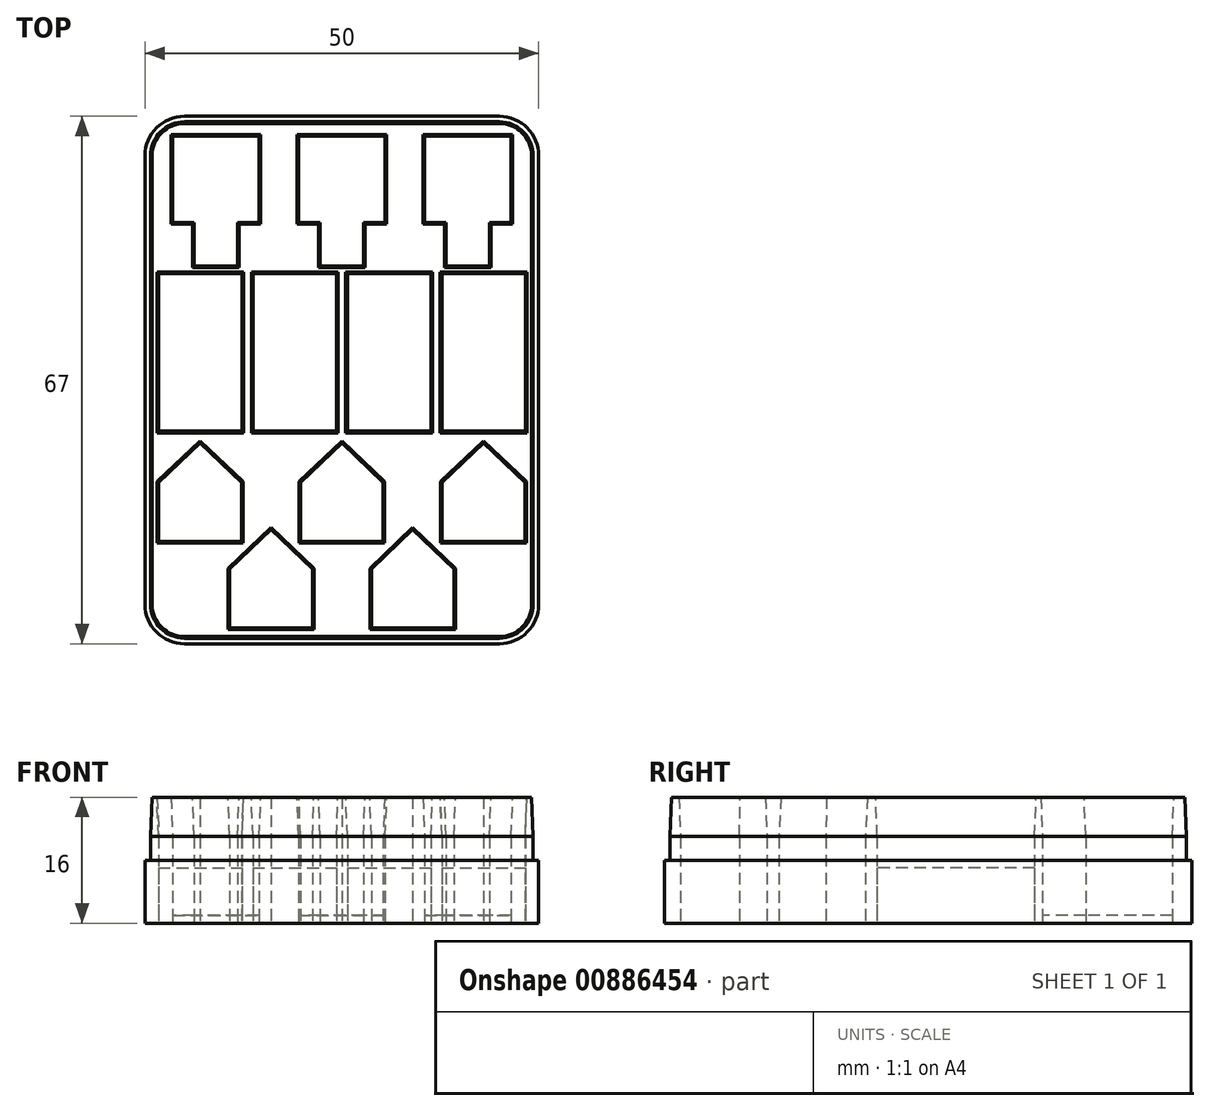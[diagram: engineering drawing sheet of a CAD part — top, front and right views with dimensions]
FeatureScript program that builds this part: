
annotation { "Feature Type Name" : "Feature", "Feature Type Description" : "" }
export const myFeature = defineFeature(function(context is Context, id is Id, definition is map)
    precondition{}
    {
        {
            var Q0;
            Q0=qCreatedBy(makeId("Top.planeOp"),FACE);
            var sketch = newSketch(context, id + "F0", { "sketchPlane" : qUnion([Q0])});
            skLineSegment(sketch, "E0.bottom", {"start": v(20, 33.5) * mm, "end": v(-20, 33.5) * mm});
            skLineSegment(sketch, "E0.top", {"start": v(20, -33.5) * mm, "end": v(-20, -33.5) * mm});
            skLineSegment(sketch, "E0.left", {"start": v(25, 28.5) * mm, "end": v(25, -28.5) * mm});
            skLineSegment(sketch, "E0.right", {"start": v(-25, 28.5) * mm, "end": v(-25, -28.5) * mm});
            skPoint(sketch, "E0.middle", {"position": v(0, 0) * mm});
            skLineSegment(sketch, "E1", {"start": v(-5.5, 31) * mm, "end": v(5.5, 31) * mm});
            skLineSegment(sketch, "E2", {"start": v(5.5, 20) * mm, "end": v(2.75, 20) * mm});
            skLineSegment(sketch, "E3", {"start": v(2.75, 20) * mm, "end": v(2.75, 14.5) * mm});
            skLineSegment(sketch, "E4", {"start": v(2.75, 14.5) * mm, "end": v(-2.75, 14.5) * mm});
            skLineSegment(sketch, "E5", {"start": v(-2.75, 14.5) * mm, "end": v(-2.75, 20) * mm});
            skLineSegment(sketch, "E6", {"start": v(-2.75, 20) * mm, "end": v(-5.5, 20) * mm});
            skLineSegment(sketch, "E7", {"start": v(-5.5, 20) * mm, "end": v(-5.5, 31) * mm});
            skLineSegment(sketch, "E8", {"start": v(5.5, 31) * mm, "end": v(5.5, 20) * mm});
            skLineSegment(sketch, "E9.1.0.0", {"start": v(10.5, 31) * mm, "end": v(21.5, 31) * mm});
            skLineSegment(sketch, "E9.1.0.1", {"start": v(18.75, 14.5) * mm, "end": v(13.25, 14.5) * mm});
            skLineSegment(sketch, "E9.1.0.2", {"start": v(21.5, 31) * mm, "end": v(21.5, 20) * mm});
            skLineSegment(sketch, "E9.1.0.3", {"start": v(21.5, 20) * mm, "end": v(18.75, 20) * mm});
            skLineSegment(sketch, "E9.1.0.4", {"start": v(18.75, 20) * mm, "end": v(18.75, 14.5) * mm});
            skLineSegment(sketch, "E9.1.0.5", {"start": v(13.25, 14.5) * mm, "end": v(13.25, 20) * mm});
            skLineSegment(sketch, "E9.1.0.6", {"start": v(10.5, 20) * mm, "end": v(10.5, 31) * mm});
            skLineSegment(sketch, "E9.1.0.7", {"start": v(13.25, 20) * mm, "end": v(10.5, 20) * mm});
            skLineSegment(sketch, "E9.direction1", {"start": v(-2.75, 14.5) * mm, "end": v(13.25, 14.5) * mm, "construction": true});
            skLineSegment(sketch, "E10.direction1", {"start": v(-2.75, 14.5) * mm, "end": v(-18.75, 14.5) * mm, "construction": true});
            skLineSegment(sketch, "E11.0.1.0", {"start": v(-13.25, 14.5) * mm, "end": v(-18.75, 14.5) * mm});
            skLineSegment(sketch, "E11.3.1.0", {"start": v(-21.5, 31) * mm, "end": v(-10.5, 31) * mm});
            skLineSegment(sketch, "E11.6.1.0", {"start": v(-21.5, 20) * mm, "end": v(-21.5, 31) * mm});
            skLineSegment(sketch, "E11.9.1.0", {"start": v(-18.75, 14.5) * mm, "end": v(-18.75, 20) * mm});
            skLineSegment(sketch, "E11.12.1.0", {"start": v(-10.5, 31) * mm, "end": v(-10.5, 20) * mm});
            skLineSegment(sketch, "E11.15.1.0", {"start": v(-10.5, 20) * mm, "end": v(-13.25, 20) * mm});
            skLineSegment(sketch, "E11.18.1.0", {"start": v(-13.25, 20) * mm, "end": v(-13.25, 14.5) * mm});
            skLineSegment(sketch, "E11.21.1.0", {"start": v(-18.75, 20) * mm, "end": v(-21.5, 20) * mm});
            skLineSegment(sketch, "E12.bottom", {"start": v(-23.3, 13.5) * mm, "end": v(-12.7, 13.5) * mm});
            skLineSegment(sketch, "E12.top", {"start": v(-23.3, -6.5) * mm, "end": v(-12.7, -6.5) * mm});
            skLineSegment(sketch, "E12.left", {"start": v(-23.3, 13.5) * mm, "end": v(-23.3, -6.5) * mm});
            skLineSegment(sketch, "E12.right", {"start": v(-12.7, 13.5) * mm, "end": v(-12.7, -6.5) * mm});
            skLineSegment(sketch, "E13.1.0.0", {"start": v(-11.3, -6.5) * mm, "end": v(-0.7, -6.5) * mm});
            skLineSegment(sketch, "E13.1.0.1", {"start": v(-11.3, 13.5) * mm, "end": v(-0.7, 13.5) * mm});
            skLineSegment(sketch, "E13.1.0.2", {"start": v(-0.7, 13.5) * mm, "end": v(-0.7, -6.5) * mm});
            skLineSegment(sketch, "E13.1.0.3", {"start": v(-11.3, 13.5) * mm, "end": v(-11.3, -6.5) * mm});
            skLineSegment(sketch, "E13.2.0.0", {"start": v(0.7, -6.5) * mm, "end": v(11.3, -6.5) * mm});
            skLineSegment(sketch, "E13.2.0.1", {"start": v(0.7, 13.5) * mm, "end": v(11.3, 13.5) * mm});
            skLineSegment(sketch, "E13.2.0.2", {"start": v(11.3, 13.5) * mm, "end": v(11.3, -6.5) * mm});
            skLineSegment(sketch, "E13.2.0.3", {"start": v(0.7, 13.5) * mm, "end": v(0.7, -6.5) * mm});
            skLineSegment(sketch, "E13.3.0.0", {"start": v(12.7, -6.5) * mm, "end": v(23.3, -6.5) * mm});
            skLineSegment(sketch, "E13.3.0.1", {"start": v(12.7, 13.5) * mm, "end": v(23.3, 13.5) * mm});
            skLineSegment(sketch, "E13.3.0.2", {"start": v(23.3, 13.5) * mm, "end": v(23.3, -6.5) * mm});
            skLineSegment(sketch, "E13.3.0.3", {"start": v(12.7, 13.5) * mm, "end": v(12.7, -6.5) * mm});
            skLineSegment(sketch, "E13.direction1", {"start": v(-23.3, -6.5) * mm, "end": v(-11.3, -6.5) * mm, "construction": true});
            skLineSegment(sketch, "E14", {"start": v(-23.25, -13) * mm, "end": v(-23.25, -20.5) * mm});
            skLineSegment(sketch, "E15", {"start": v(-23.25, -20.5) * mm, "end": v(-12.75, -20.5) * mm});
            skLineSegment(sketch, "E16", {"start": v(-12.75, -20.5) * mm, "end": v(-12.75, -13) * mm});
            skLineSegment(sketch, "E17", {"start": v(-12.75, -13) * mm, "end": v(-18, -8) * mm});
            skPoint(sketch, "E17.endSnap0", {"position": v(-18, -20.5) * mm});
            skLineSegment(sketch, "E18", {"start": v(-18, -8) * mm, "end": v(-23.25, -13) * mm});
            skPoint(sketch, "E19.1.0.0", {"position": v(0, -20.5) * mm});
            skLineSegment(sketch, "E19.1.0.1", {"start": v(-5.25, -20.5) * mm, "end": v(5.25, -20.5) * mm});
            skLineSegment(sketch, "E19.1.0.2", {"start": v(5.25, -20.5) * mm, "end": v(5.25, -13) * mm});
            skLineSegment(sketch, "E19.1.0.3", {"start": v(5.25, -13) * mm, "end": v(0, -8) * mm});
            skLineSegment(sketch, "E19.1.0.4", {"start": v(-5.25, -13) * mm, "end": v(-5.25, -20.5) * mm});
            skLineSegment(sketch, "E19.1.0.5", {"start": v(0, -8) * mm, "end": v(-5.25, -13) * mm});
            skPoint(sketch, "E19.2.0.0", {"position": v(18, -20.5) * mm});
            skLineSegment(sketch, "E19.2.0.1", {"start": v(12.75, -20.5) * mm, "end": v(23.25, -20.5) * mm});
            skLineSegment(sketch, "E19.2.0.2", {"start": v(23.25, -20.5) * mm, "end": v(23.25, -13) * mm});
            skLineSegment(sketch, "E19.2.0.3", {"start": v(23.25, -13) * mm, "end": v(18, -8) * mm});
            skLineSegment(sketch, "E19.2.0.4", {"start": v(12.75, -13) * mm, "end": v(12.75, -20.5) * mm});
            skLineSegment(sketch, "E19.2.0.5", {"start": v(18, -8) * mm, "end": v(12.75, -13) * mm});
            skLineSegment(sketch, "E19.direction1", {"start": v(-23.25, -20.5) * mm, "end": v(-5.25, -20.5) * mm, "construction": true});
            skLineSegment(sketch, "E20.1.0.0", {"start": v(-3.75, -24) * mm, "end": v(-9, -19) * mm});
            skLineSegment(sketch, "E20.1.0.1", {"start": v(-3.75, -31.5) * mm, "end": v(-3.75, -24) * mm});
            skLineSegment(sketch, "E20.1.0.2", {"start": v(-14.25, -24) * mm, "end": v(-14.25, -31.5) * mm});
            skLineSegment(sketch, "E20.1.0.3", {"start": v(-9, -19) * mm, "end": v(-14.25, -24) * mm});
            skLineSegment(sketch, "E20.1.0.4", {"start": v(-14.25, -31.5) * mm, "end": v(-3.75, -31.5) * mm});
            skPoint(sketch, "E20.1.0.5", {"position": v(-9, -31.5) * mm});
            skLineSegment(sketch, "E20.direction1", {"start": v(-23.25, -20.5) * mm, "end": v(-14.25, -31.5) * mm, "construction": true});
            skLineSegment(sketch, "E21.1.0.0", {"start": v(14.25, -24) * mm, "end": v(9, -19) * mm});
            skLineSegment(sketch, "E21.1.0.1", {"start": v(3.75, -24) * mm, "end": v(3.75, -31.5) * mm});
            skPoint(sketch, "E21.1.0.2", {"position": v(9, -31.5) * mm});
            skLineSegment(sketch, "E21.1.0.3", {"start": v(14.25, -31.5) * mm, "end": v(14.25, -24) * mm});
            skLineSegment(sketch, "E21.1.0.4", {"start": v(9, -19) * mm, "end": v(3.75, -24) * mm});
            skLineSegment(sketch, "E21.1.0.5", {"start": v(3.75, -31.5) * mm, "end": v(14.25, -31.5) * mm});
            skLineSegment(sketch, "E21.direction1", {"start": v(-23.25, -20.5) * mm, "end": v(3.75, -31.5) * mm, "construction": true});
            skPoint(sketch, "E22.visualSharp", {"position": v(-25, 33.5) * mm});
            skArc(sketch, "E22.filletArc", {"start": v(-20, 33.5) * mm, "mid": v(-23.54, 32.04) * mm, "end": v(-25, 28.5) * mm});
            skPoint(sketch, "E23.visualSharp", {"position": v(25, 33.5) * mm});
            skArc(sketch, "E23.filletArc", {"start": v(25, 28.5) * mm, "mid": v(23.54, 32.04) * mm, "end": v(20, 33.5) * mm});
            skPoint(sketch, "E24.visualSharp", {"position": v(25, -33.5) * mm});
            skArc(sketch, "E24.filletArc", {"start": v(20, -33.5) * mm, "mid": v(23.54, -32.04) * mm, "end": v(25, -28.5) * mm});
            skPoint(sketch, "E25.visualSharp", {"position": v(-25, -33.5) * mm});
            skArc(sketch, "E25.filletArc", {"start": v(-25, -28.5) * mm, "mid": v(-23.54, -32.04) * mm, "end": v(-20, -33.5) * mm});
            skLineSegment(sketch, "E26.bottom", {"start": v(20, 32.8) * mm, "end": v(-20, 32.8) * mm});
            skLineSegment(sketch, "E26.top", {"start": v(20, -32.8) * mm, "end": v(-20, -32.8) * mm});
            skLineSegment(sketch, "E26.left", {"start": v(24.3, 28.5) * mm, "end": v(24.3, -28.5) * mm});
            skLineSegment(sketch, "E26.right", {"start": v(-24.3, 28.5) * mm, "end": v(-24.3, -28.5) * mm});
            skPoint(sketch, "E27.visualSharp", {"position": v(24.3, 32.8) * mm});
            skArc(sketch, "E27.filletArc", {"start": v(24.3, 28.5) * mm, "mid": v(23.04, 31.54) * mm, "end": v(20, 32.8) * mm});
            skPoint(sketch, "E28.visualSharp", {"position": v(-24.3, 32.8) * mm});
            skArc(sketch, "E28.filletArc", {"start": v(-20, 32.8) * mm, "mid": v(-23.04, 31.54) * mm, "end": v(-24.3, 28.5) * mm});
            skPoint(sketch, "E29.visualSharp", {"position": v(-24.3, -32.8) * mm});
            skArc(sketch, "E29.filletArc", {"start": v(-24.3, -28.5) * mm, "mid": v(-23.04, -31.54) * mm, "end": v(-20, -32.8) * mm});
            skPoint(sketch, "E30.visualSharp", {"position": v(24.3, -32.8) * mm});
            skArc(sketch, "E30.filletArc", {"start": v(20, -32.8) * mm, "mid": v(23.04, -31.54) * mm, "end": v(24.3, -28.5) * mm});
            skSolve(sketch);
        }
        {
            var Q0;
            Q0=makeQuery(id+"F0.imprint","IMPRINT",FACE,{"disambiguationData":[TD([[makeQuery(id+"F0.imprint","IMPRINT",EDGE,{"derivedFrom":sQuery(id+"F0.wireOp",EDGE,"E11.0.1.0")}),-1.0]])]});
            var Q1;
            Q1=makeQuery(id+"F0.imprint","IMPRINT",FACE,{"disambiguationData":[TD([[makeQuery(id+"F0.imprint","IMPRINT",EDGE,{"derivedFrom":sQuery(id+"F0.wireOp",EDGE,"E1")}),-1.0]])]});
            var Q2;
            Q2=makeQuery(id+"F0.imprint","IMPRINT",FACE,{"disambiguationData":[TD([[makeQuery(id+"F0.imprint","IMPRINT",EDGE,{"derivedFrom":sQuery(id+"F0.wireOp",EDGE,"E9.1.0.0")}),-1.0]])]});
            extrude(context, id + "F1", {"entities" : qUnion([Q0, Q1, Q2]), "depth" : 1 * mm, "offsetDistance" : 25 * mm});
        }
        {
            var Q0;
            Q0=makeQuery(id+"F0.imprint","IMPRINT",FACE,{"disambiguationData":[TD([[makeQuery(id+"F0.imprint","IMPRINT",EDGE,{"derivedFrom":sQuery(id+"F0.wireOp",EDGE,"E12.bottom")}),-1.0]])]});
            var Q1;
            Q1=makeQuery(id+"F0.imprint","IMPRINT",FACE,{"disambiguationData":[TD([[makeQuery(id+"F0.imprint","IMPRINT",EDGE,{"derivedFrom":sQuery(id+"F0.wireOp",EDGE,"E13.1.0.0")}),1.0]])]});
            var Q2;
            Q2=makeQuery(id+"F0.imprint","IMPRINT",FACE,{"disambiguationData":[TD([[makeQuery(id+"F0.imprint","IMPRINT",EDGE,{"derivedFrom":sQuery(id+"F0.wireOp",EDGE,"E13.2.0.0")}),1.0]])]});
            var Q3;
            Q3=makeQuery(id+"F0.imprint","IMPRINT",FACE,{"disambiguationData":[TD([[makeQuery(id+"F0.imprint","IMPRINT",EDGE,{"derivedFrom":sQuery(id+"F0.wireOp",EDGE,"E13.3.0.0")}),1.0]])]});
            extrude(context, id + "F2", {"entities" : qUnion([Q0, Q1, Q2, Q3]), "depth" : 7 * mm, "offsetDistance" : 25 * mm});
        }
        {
            var Q0;
            Q0=makeQuery(id+"F0.imprint","IMPRINT",FACE,{"disambiguationData":[TD([[makeQuery(id+"F0.imprint","IMPRINT",EDGE,{"derivedFrom":sQuery(id+"F0.wireOp",EDGE,"E14")}),1.0]])]});
            var Q1;
            Q1=makeQuery(id+"F0.imprint","IMPRINT",FACE,{"disambiguationData":[TD([[makeQuery(id+"F0.imprint","IMPRINT",EDGE,{"derivedFrom":sQuery(id+"F0.wireOp",EDGE,"E19.1.0.1")}),1.0]])]});
            var Q2;
            Q2=makeQuery(id+"F0.imprint","IMPRINT",FACE,{"disambiguationData":[TD([[makeQuery(id+"F0.imprint","IMPRINT",EDGE,{"derivedFrom":sQuery(id+"F0.wireOp",EDGE,"E19.2.0.1")}),1.0]])]});
            var Q3;
            Q3=makeQuery(id+"F0.imprint","IMPRINT",FACE,{"disambiguationData":[TD([[makeQuery(id+"F0.imprint","IMPRINT",EDGE,{"derivedFrom":sQuery(id+"F0.wireOp",EDGE,"E21.1.0.0")}),1.0]])]});
            var Q4;
            Q4=makeQuery(id+"F0.imprint","IMPRINT",FACE,{"disambiguationData":[TD([[makeQuery(id+"F0.imprint","IMPRINT",EDGE,{"derivedFrom":sQuery(id+"F0.wireOp",EDGE,"E20.1.0.0")}),1.0]])]});
            extrude(context, id + "F3", {"entities" : qUnion([Q0, Q1, Q2, Q3, Q4]), "depth" : 11 * mm, "offsetDistance" : 25 * mm});
        }
        {
            var Q0;
            Q0=makeQuery(id+"F0.imprint","IMPRINT",FACE,{"disambiguationData":[TD([[makeQuery(id+"F0.imprint","IMPRINT",EDGE,{"derivedFrom":sQuery(id+"F0.wireOp",EDGE,"E1")}),1.0]])]});
            extrude(context, id + "F4", {"entities" : qUnion([Q0]), "depth" : 16 * mm, "offsetDistance" : 25 * mm});
        }
        {
            var Q0;
            Q0=makeQuery(id+"F0.imprint","IMPRINT",FACE,{"disambiguationData":[TD([[makeQuery(id+"F0.imprint","IMPRINT",EDGE,{"derivedFrom":sQuery(id+"F0.wireOp",EDGE,"E0.bottom")}),1.0]])]});
            extrude(context, id + "F5", {"entities" : qUnion([Q0]), "operationType" : NewBodyOperationType.ADD, "depth" : 8 * mm, "offsetDistance" : 25 * mm});
        }
        {
            var Q0;
            Q0=makeQuery(id+"F4.opExtrude","CAP_FACE",FACE,{"disambiguationData":[OSD([sQuery(id+"F0.wireOp",EDGE,"E1"),sQuery(id+"F0.wireOp",EDGE,"E2"),sQuery(id+"F0.wireOp",EDGE,"E3"),sQuery(id+"F0.wireOp",EDGE,"E4"),sQuery(id+"F0.wireOp",EDGE,"E5"),sQuery(id+"F0.wireOp",EDGE,"E6"),sQuery(id+"F0.wireOp",EDGE,"E7"),sQuery(id+"F0.wireOp",EDGE,"E8"),sQuery(id+"F0.wireOp",EDGE,"E9.1.0.0"),sQuery(id+"F0.wireOp",EDGE,"E9.1.0.1"),sQuery(id+"F0.wireOp",EDGE,"E9.1.0.2"),sQuery(id+"F0.wireOp",EDGE,"E9.1.0.3"),sQuery(id+"F0.wireOp",EDGE,"E9.1.0.4"),sQuery(id+"F0.wireOp",EDGE,"E9.1.0.5"),sQuery(id+"F0.wireOp",EDGE,"E9.1.0.6"),sQuery(id+"F0.wireOp",EDGE,"E9.1.0.7"),sQuery(id+"F0.wireOp",EDGE,"E11.0.1.0"),sQuery(id+"F0.wireOp",EDGE,"E11.3.1.0"),sQuery(id+"F0.wireOp",EDGE,"E11.6.1.0"),sQuery(id+"F0.wireOp",EDGE,"E11.9.1.0"),sQuery(id+"F0.wireOp",EDGE,"E11.12.1.0"),sQuery(id+"F0.wireOp",EDGE,"E11.15.1.0"),sQuery(id+"F0.wireOp",EDGE,"E11.18.1.0"),sQuery(id+"F0.wireOp",EDGE,"E11.21.1.0"),sQuery(id+"F0.wireOp",EDGE,"E12.bottom"),sQuery(id+"F0.wireOp",EDGE,"E12.top"),sQuery(id+"F0.wireOp",EDGE,"E12.left"),sQuery(id+"F0.wireOp",EDGE,"E12.right"),sQuery(id+"F0.wireOp",EDGE,"E13.1.0.0"),sQuery(id+"F0.wireOp",EDGE,"E13.1.0.1"),sQuery(id+"F0.wireOp",EDGE,"E13.1.0.2"),sQuery(id+"F0.wireOp",EDGE,"E13.1.0.3"),sQuery(id+"F0.wireOp",EDGE,"E13.2.0.0"),sQuery(id+"F0.wireOp",EDGE,"E13.2.0.1"),sQuery(id+"F0.wireOp",EDGE,"E13.2.0.2"),sQuery(id+"F0.wireOp",EDGE,"E13.2.0.3"),sQuery(id+"F0.wireOp",EDGE,"E13.3.0.0"),sQuery(id+"F0.wireOp",EDGE,"E13.3.0.1"),sQuery(id+"F0.wireOp",EDGE,"E13.3.0.2"),sQuery(id+"F0.wireOp",EDGE,"E13.3.0.3"),sQuery(id+"F0.wireOp",EDGE,"E14"),sQuery(id+"F0.wireOp",EDGE,"E15"),sQuery(id+"F0.wireOp",EDGE,"E16"),sQuery(id+"F0.wireOp",EDGE,"E17"),sQuery(id+"F0.wireOp",EDGE,"E18"),sQuery(id+"F0.wireOp",EDGE,"E19.1.0.1"),sQuery(id+"F0.wireOp",EDGE,"E19.1.0.2"),sQuery(id+"F0.wireOp",EDGE,"E19.1.0.3"),sQuery(id+"F0.wireOp",EDGE,"E19.1.0.4"),sQuery(id+"F0.wireOp",EDGE,"E19.1.0.5"),sQuery(id+"F0.wireOp",EDGE,"E19.2.0.1"),sQuery(id+"F0.wireOp",EDGE,"E19.2.0.2"),sQuery(id+"F0.wireOp",EDGE,"E19.2.0.3"),sQuery(id+"F0.wireOp",EDGE,"E19.2.0.4"),sQuery(id+"F0.wireOp",EDGE,"E19.2.0.5"),sQuery(id+"F0.wireOp",EDGE,"E20.1.0.0"),sQuery(id+"F0.wireOp",EDGE,"E20.1.0.1"),sQuery(id+"F0.wireOp",EDGE,"E20.1.0.2"),sQuery(id+"F0.wireOp",EDGE,"E20.1.0.3"),sQuery(id+"F0.wireOp",EDGE,"E20.1.0.4"),sQuery(id+"F0.wireOp",EDGE,"E21.1.0.0"),sQuery(id+"F0.wireOp",EDGE,"E21.1.0.1"),sQuery(id+"F0.wireOp",EDGE,"E21.1.0.3"),sQuery(id+"F0.wireOp",EDGE,"E21.1.0.4"),sQuery(id+"F0.wireOp",EDGE,"E21.1.0.5"),sQuery(id+"F0.wireOp",EDGE,"E26.bottom"),sQuery(id+"F0.wireOp",EDGE,"E26.top"),sQuery(id+"F0.wireOp",EDGE,"E26.left"),sQuery(id+"F0.wireOp",EDGE,"E26.right"),sQuery(id+"F0.wireOp",EDGE,"E27.filletArc"),sQuery(id+"F0.wireOp",EDGE,"E28.filletArc"),sQuery(id+"F0.wireOp",EDGE,"E29.filletArc"),sQuery(id+"F0.wireOp",EDGE,"E30.filletArc")])],"isStart":false});
            chamfer(context, id + "F6", {"entities" : qUnion([Q0]), "chamferType" : ChamferType.TWO_OFFSETS, "width1" : 0.2 * mm, "oppositeDirection" : false, "width2" : 5 * mm, "tangentPropagation" : true});
        }
    });
